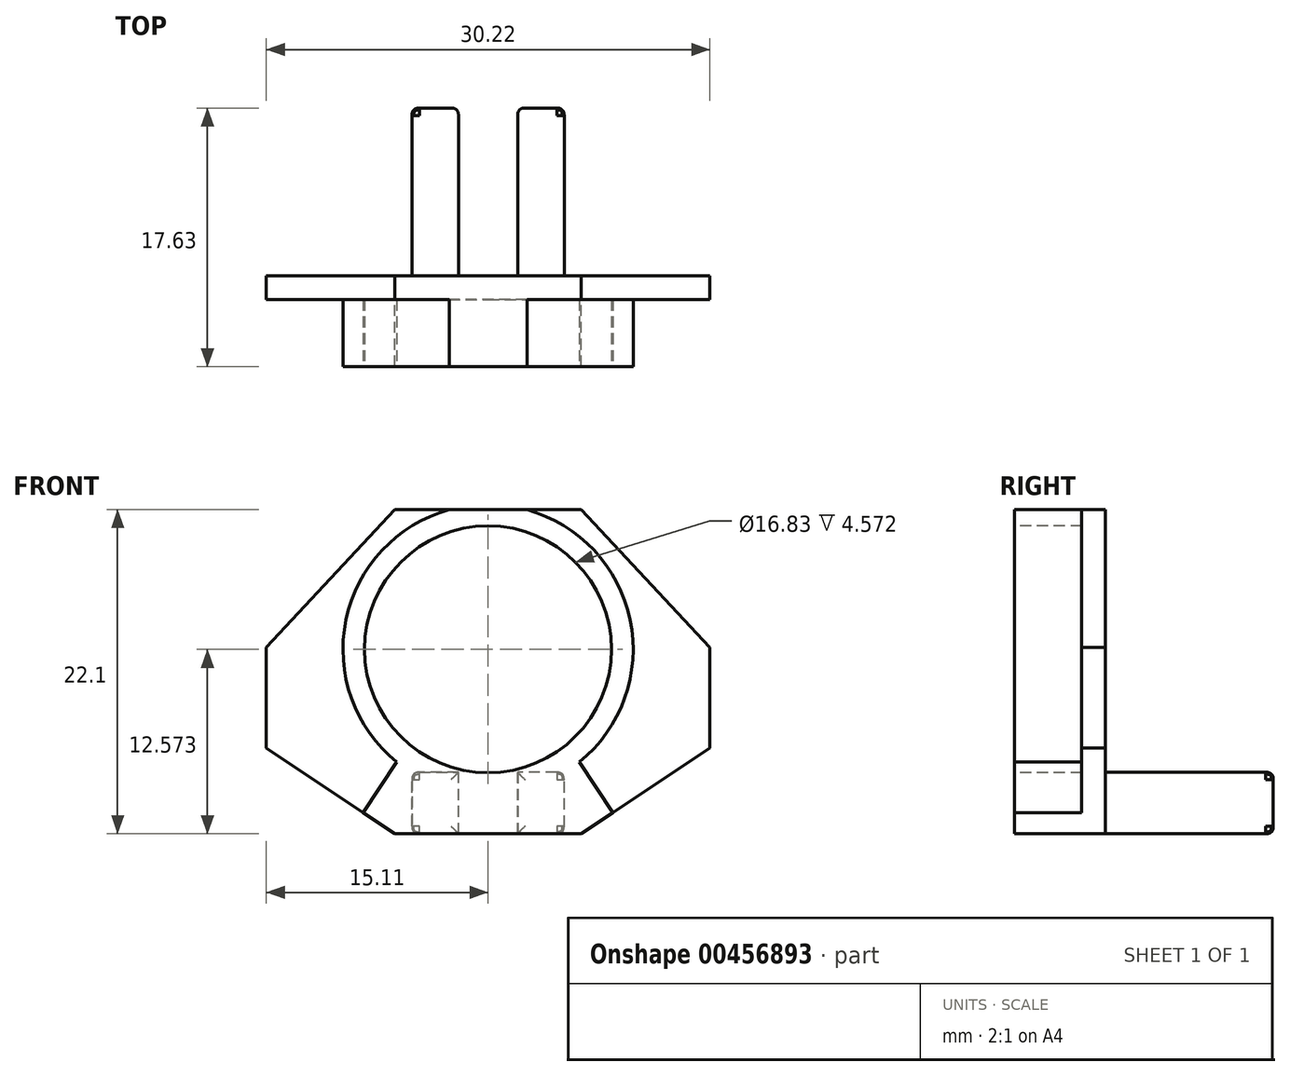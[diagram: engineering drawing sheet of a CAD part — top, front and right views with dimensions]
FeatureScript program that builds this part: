
annotation { "Feature Type Name" : "Feature", "Feature Type Description" : "" }
export const myFeature = defineFeature(function(context is Context, id is Id, definition is map)
    precondition{}
    {
        {
            var Q0;
            Q0=qCreatedBy(makeId("Front.planeOp"),FACE);
            var sketch = newSketch(context, id + "F0", { "sketchPlane" : qUnion([Q0])});
            skLineSegment(sketch, "E0", {"start": v(0, 0) * mm, "end": v(0, 22.1) * mm, "construction": true});
            skLineSegment(sketch, "E1", {"start": v(0, 0) * mm, "end": v(6.35, 0) * mm});
            skLineSegment(sketch, "E2", {"start": v(6.35, 0) * mm, "end": v(15.11, 5.84) * mm});
            skLineSegment(sketch, "E3", {"start": v(15.11, 5.84) * mm, "end": v(15.11, 12.7) * mm});
            skLineSegment(sketch, "E4", {"start": v(15.11, 12.7) * mm, "end": v(6.35, 22.1) * mm});
            skLineSegment(sketch, "E5", {"start": v(6.35, 22.1) * mm, "end": v(0, 22.1) * mm});
            skLineSegment(sketch, "E6.MirrorCS", {"start": v(-6.35, 22.1) * mm, "end": v(0, 22.1) * mm});
            skLineSegment(sketch, "E7.MirrorCS", {"start": v(-15.11, 12.7) * mm, "end": v(-6.35, 22.1) * mm});
            skLineSegment(sketch, "E8.MirrorCS", {"start": v(-15.11, 5.84) * mm, "end": v(-15.11, 12.7) * mm});
            skLineSegment(sketch, "E9.MirrorCS", {"start": v(-6.35, 0) * mm, "end": v(-15.11, 5.84) * mm});
            skLineSegment(sketch, "E10.MirrorCS", {"start": v(0, 0) * mm, "end": v(-6.35, 0) * mm});
            skSolve(sketch);
        }
        {
            var Q0;
            Q0 = qSketchRegion(id + "F0", true);
            extrude(context, id + "F1", {"entities" : qUnion([Q0]), "depth" : 6.2 * mm});
        }
        {
            var Q0;
            Q0=makeQuery(id+"F1.opExtrude","CAP_FACE",FACE,{"disambiguationData":[OSD([sQuery(id+"F0.wireOp",EDGE,"E1"),sQuery(id+"F0.wireOp",EDGE,"E2"),sQuery(id+"F0.wireOp",EDGE,"E3"),sQuery(id+"F0.wireOp",EDGE,"E4"),sQuery(id+"F0.wireOp",EDGE,"E5"),sQuery(id+"F0.wireOp",EDGE,"E6.MirrorCS"),sQuery(id+"F0.wireOp",EDGE,"E7.MirrorCS"),sQuery(id+"F0.wireOp",EDGE,"E8.MirrorCS"),sQuery(id+"F0.wireOp",EDGE,"E9.MirrorCS"),sQuery(id+"F0.wireOp",EDGE,"E10.MirrorCS")])],"isStart":false});
            var sketch = newSketch(context, id + "F2", { "sketchPlane" : qUnion([Q0])});
            skCircle(sketch, "E11", {"center": v(0, 12.57) * mm, "radius": 8.41 * mm});
            skLineSegment(sketch, "E12", {"start": v(-6.35, 22.1) * mm, "end": v(-15.11, 12.7) * mm});
            skLineSegment(sketch, "E13", {"start": v(-15.11, 12.7) * mm, "end": v(-15.11, 5.84) * mm});
            skLineSegment(sketch, "E14", {"start": v(-15.11, 5.84) * mm, "end": v(-8.5, 1.44) * mm});
            skLineSegment(sketch, "E15", {"start": v(8.5, 1.44) * mm, "end": v(15.11, 5.84) * mm});
            skLineSegment(sketch, "E16", {"start": v(15.11, 5.84) * mm, "end": v(15.11, 12.7) * mm});
            skLineSegment(sketch, "E17", {"start": v(15.11, 12.7) * mm, "end": v(6.35, 22.1) * mm});
            skLineSegment(sketch, "E18", {"start": v(6.35, 22.1) * mm, "end": v(-6.35, 22.1) * mm});
            skArc(sketch, "E19", {"start": v(6.21, 4.88) * mm, "mid": v(0, 22.46) * mm, "end": v(-6.21, 4.88) * mm});
            skLineSegment(sketch, "E20", {"start": v(8.5, 1.44) * mm, "end": v(6.21, 4.88) * mm});
            skLineSegment(sketch, "E21", {"start": v(-6.21, 4.88) * mm, "end": v(-8.5, 1.44) * mm});
            skLineSegment(sketch, "E22", {"start": v(0, 0) * mm, "end": v(0, 2.69) * mm, "construction": true});
            skSolve(sketch);
        }
        {
            var Q0;
            Q0=makeQuery(id+"F2.imprint","IMPRINT",FACE,{"disambiguationData":[TD([[makeQuery(id+"F2.imprint","IMPRINT",EDGE,{"derivedFrom":sQuery(id+"F2.wireOp",EDGE,"E15")}),1.0]])]});
            var Q1;
            Q1=makeQuery(id+"F2.imprint","IMPRINT",FACE,{"disambiguationData":[TD([[makeQuery(id+"F2.imprint","IMPRINT",EDGE,{"derivedFrom":sQuery(id+"F2.wireOp",EDGE,"E11")}),1.0]])]});
            var Q2;
            {var subQ1=sQuery(id+"F2.wireOp",EDGE,"E12");Q2=makeQuery(id+"F2.imprint","IMPRINT",FACE,{"disambiguationData":[TD([[makeQuery(id+"F2.imprint","IMPRINT",EDGE,{"derivedFrom":subQ1}),-1.0]])]});}
            var Q3;
            Q3=makeQuery(id+"F1.opExtrude","CAP_FACE",FACE,{"disambiguationData":[OSD([sQuery(id+"F0.wireOp",EDGE,"E1"),sQuery(id+"F0.wireOp",EDGE,"E2"),sQuery(id+"F0.wireOp",EDGE,"E3"),sQuery(id+"F0.wireOp",EDGE,"E4"),sQuery(id+"F0.wireOp",EDGE,"E5"),sQuery(id+"F0.wireOp",EDGE,"E6.MirrorCS"),sQuery(id+"F0.wireOp",EDGE,"E7.MirrorCS"),sQuery(id+"F0.wireOp",EDGE,"E8.MirrorCS"),sQuery(id+"F0.wireOp",EDGE,"E9.MirrorCS"),sQuery(id+"F0.wireOp",EDGE,"E10.MirrorCS")])],"isStart":true});
            extrude(context, id + "F3", {"entities" : qUnion([Q0, Q1, Q2]), "operationType" : NewBodyOperationType.REMOVE, "oppositeDirection" : true, "endBoundEntityFace" : qUnion([Q3]), "depth" : 4.57 * mm});
        }
        {
            var Q0;
            Q0=makeQuery(id+"F1.opExtrude","CAP_FACE",FACE,{"disambiguationData":[OSD([sQuery(id+"F0.wireOp",EDGE,"E1"),sQuery(id+"F0.wireOp",EDGE,"E2"),sQuery(id+"F0.wireOp",EDGE,"E3"),sQuery(id+"F0.wireOp",EDGE,"E4"),sQuery(id+"F0.wireOp",EDGE,"E5"),sQuery(id+"F0.wireOp",EDGE,"E6.MirrorCS"),sQuery(id+"F0.wireOp",EDGE,"E7.MirrorCS"),sQuery(id+"F0.wireOp",EDGE,"E8.MirrorCS"),sQuery(id+"F0.wireOp",EDGE,"E9.MirrorCS"),sQuery(id+"F0.wireOp",EDGE,"E10.MirrorCS")])],"isStart":true});
            var sketch = newSketch(context, id + "F4", { "sketchPlane" : qUnion([Q0])});
            skLineSegment(sketch, "E23", {"start": v(0, 0) * mm, "end": v(0, 22.1) * mm, "construction": true});
            skLineSegment(sketch, "E24.bottom", {"start": v(5.19, 0) * mm, "end": v(2.01, 0) * mm});
            skLineSegment(sketch, "E24.top", {"start": v(5.19, 4.2) * mm, "end": v(2.01, 4.2) * mm});
            skLineSegment(sketch, "E24.left", {"start": v(5.19, 0) * mm, "end": v(5.19, 4.2) * mm});
            skLineSegment(sketch, "E24.right", {"start": v(2.01, 0) * mm, "end": v(2.01, 4.2) * mm});
            skLineSegment(sketch, "E25.MirrorCS", {"start": v(-5.19, 4.2) * mm, "end": v(-2.01, 4.2) * mm});
            skLineSegment(sketch, "E26.MirrorCS", {"start": v(-2.01, 0) * mm, "end": v(-2.01, 4.2) * mm});
            skLineSegment(sketch, "E27.MirrorCS", {"start": v(-5.19, 0) * mm, "end": v(-2.01, 0) * mm});
            skLineSegment(sketch, "E28.MirrorCS", {"start": v(-5.19, 0) * mm, "end": v(-5.19, 4.2) * mm});
            skSolve(sketch);
        }
        {
            var Q0;
            Q0=makeQuery(id+"F4.imprint","IMPRINT",FACE,{"disambiguationData":[TD([[makeQuery(id+"F4.imprint","IMPRINT",EDGE,{"derivedFrom":sQuery(id+"F4.wireOp",EDGE,"E25.MirrorCS")}),-1.0]])]});
            var Q1;
            Q1=makeQuery(id+"F4.imprint","IMPRINT",FACE,{"disambiguationData":[TD([[makeQuery(id+"F4.imprint","IMPRINT",EDGE,{"derivedFrom":sQuery(id+"F4.wireOp",EDGE,"E24.bottom")}),1.0]])]});
            extrude(context, id + "F5", {"entities" : qUnion([Q0, Q1]), "operationType" : NewBodyOperationType.ADD, "depth" : 11.43 * mm});
        }
        {
            var Q0;
            Q0=makeQuery(id+"F5.opExtrude","SWEPT_EDGE",EDGE,{"disambiguationData":[OSD([sQuery(id+"F4.wireOp",EDGE,"E25.MirrorCS"),sQuery(id+"F4.wireOp",EDGE,"E28.MirrorCS")])]});
            var Q1;
            Q1=makeQuery(id+"F5.opExtrude","SWEPT_EDGE",EDGE,{"disambiguationData":[OSD([sQuery(id+"F0.wireOp",EDGE,"E1"),sQuery(id+"F0.wireOp",EDGE,"E10.MirrorCS"),sQuery(id+"F4.wireOp",EDGE,"E27.MirrorCS"),sQuery(id+"F4.wireOp",EDGE,"E28.MirrorCS")])]});
            var Q2;
            Q2=makeQuery(id+"F5.opExtrude","SWEPT_EDGE",EDGE,{"disambiguationData":[OSD([sQuery(id+"F4.wireOp",EDGE,"E24.top"),sQuery(id+"F4.wireOp",EDGE,"E24.left")])]});
            var Q3;
            Q3=makeQuery(id+"F5.opExtrude","SWEPT_EDGE",EDGE,{"disambiguationData":[OSD([sQuery(id+"F0.wireOp",EDGE,"E1"),sQuery(id+"F0.wireOp",EDGE,"E10.MirrorCS"),sQuery(id+"F4.wireOp",EDGE,"E24.bottom"),sQuery(id+"F4.wireOp",EDGE,"E24.left")])]});
            var Q4;
            Q4=makeQuery(id+"F5.opExtrude","CAP_EDGE",EDGE,{"disambiguationData":[OSD([sQuery(id+"F4.wireOp",EDGE,"E24.bottom")])],"isStart":false});
            var Q5;
            Q5=makeQuery(id+"F5.opExtrude","CAP_EDGE",EDGE,{"disambiguationData":[OSD([sQuery(id+"F4.wireOp",EDGE,"E24.right")])],"isStart":false});
            var Q6;
            Q6=makeQuery(id+"F5.opExtrude","CAP_EDGE",EDGE,{"disambiguationData":[OSD([sQuery(id+"F4.wireOp",EDGE,"E24.top")])],"isStart":false});
            var Q7;
            Q7=makeQuery(id+"F5.opExtrude","CAP_EDGE",EDGE,{"disambiguationData":[OSD([sQuery(id+"F4.wireOp",EDGE,"E26.MirrorCS")])],"isStart":false});
            var Q8;
            Q8=makeQuery(id+"F5.opExtrude","CAP_EDGE",EDGE,{"disambiguationData":[OSD([sQuery(id+"F4.wireOp",EDGE,"E28.MirrorCS")])],"isStart":false});
            var Q9;
            Q9=makeQuery(id+"F5.opExtrude","CAP_EDGE",EDGE,{"disambiguationData":[OSD([sQuery(id+"F4.wireOp",EDGE,"E25.MirrorCS")])],"isStart":false});
            var Q10;
            Q10=makeQuery(id+"F5.opExtrude","CAP_EDGE",EDGE,{"disambiguationData":[OSD([sQuery(id+"F4.wireOp",EDGE,"E27.MirrorCS")])],"isStart":false});
            var Q11;
            Q11=makeQuery(id+"F5.opExtrude","CAP_EDGE",EDGE,{"disambiguationData":[OSD([sQuery(id+"F4.wireOp",EDGE,"E24.left")])],"isStart":false});
            var Q12;
            Q12=makeQuery(id+"F5.opExtrude","CAP_EDGE",EDGE,{"disambiguationData":[OSD([sQuery(id+"F4.wireOp",EDGE,"E26.MirrorCS")])],"isStart":true});
            var Q13;
            Q13=makeQuery(id+"F5.opExtrude","CAP_EDGE",EDGE,{"disambiguationData":[OSD([sQuery(id+"F4.wireOp",EDGE,"E24.left")])],"isStart":true});
            var Q14;
            Q14=makeQuery(id+"F5.opExtrude","CAP_EDGE",EDGE,{"disambiguationData":[OSD([sQuery(id+"F4.wireOp",EDGE,"E24.top")])],"isStart":true});
            var Q15;
            Q15=makeQuery(id+"F5.opExtrude","CAP_EDGE",EDGE,{"disambiguationData":[OSD([sQuery(id+"F4.wireOp",EDGE,"E25.MirrorCS")])],"isStart":true});
            var Q16;
            Q16=makeQuery(id+"F5.opExtrude","CAP_EDGE",EDGE,{"disambiguationData":[OSD([sQuery(id+"F4.wireOp",EDGE,"E28.MirrorCS")])],"isStart":true});
            var Q17;
            Q17=makeQuery(id+"F5.opExtrude","CAP_EDGE",EDGE,{"disambiguationData":[OSD([sQuery(id+"F4.wireOp",EDGE,"E24.right")])],"isStart":true});
            fillet(context, id + "F6", {"entities" : qUnion([Q0, Q1, Q2, Q3, Q4, Q5, Q6, Q7, Q8, Q9, Q10, Q11, Q12, Q13, Q14, Q15, Q16, Q17]), "radius" : 0.5 * mm, "tangentPropagation" : true, "rho" : 0.5, "crossSection" : FilletCrossSection.CONIC, "allowEdgeOverflow" : false});
        }
    });
